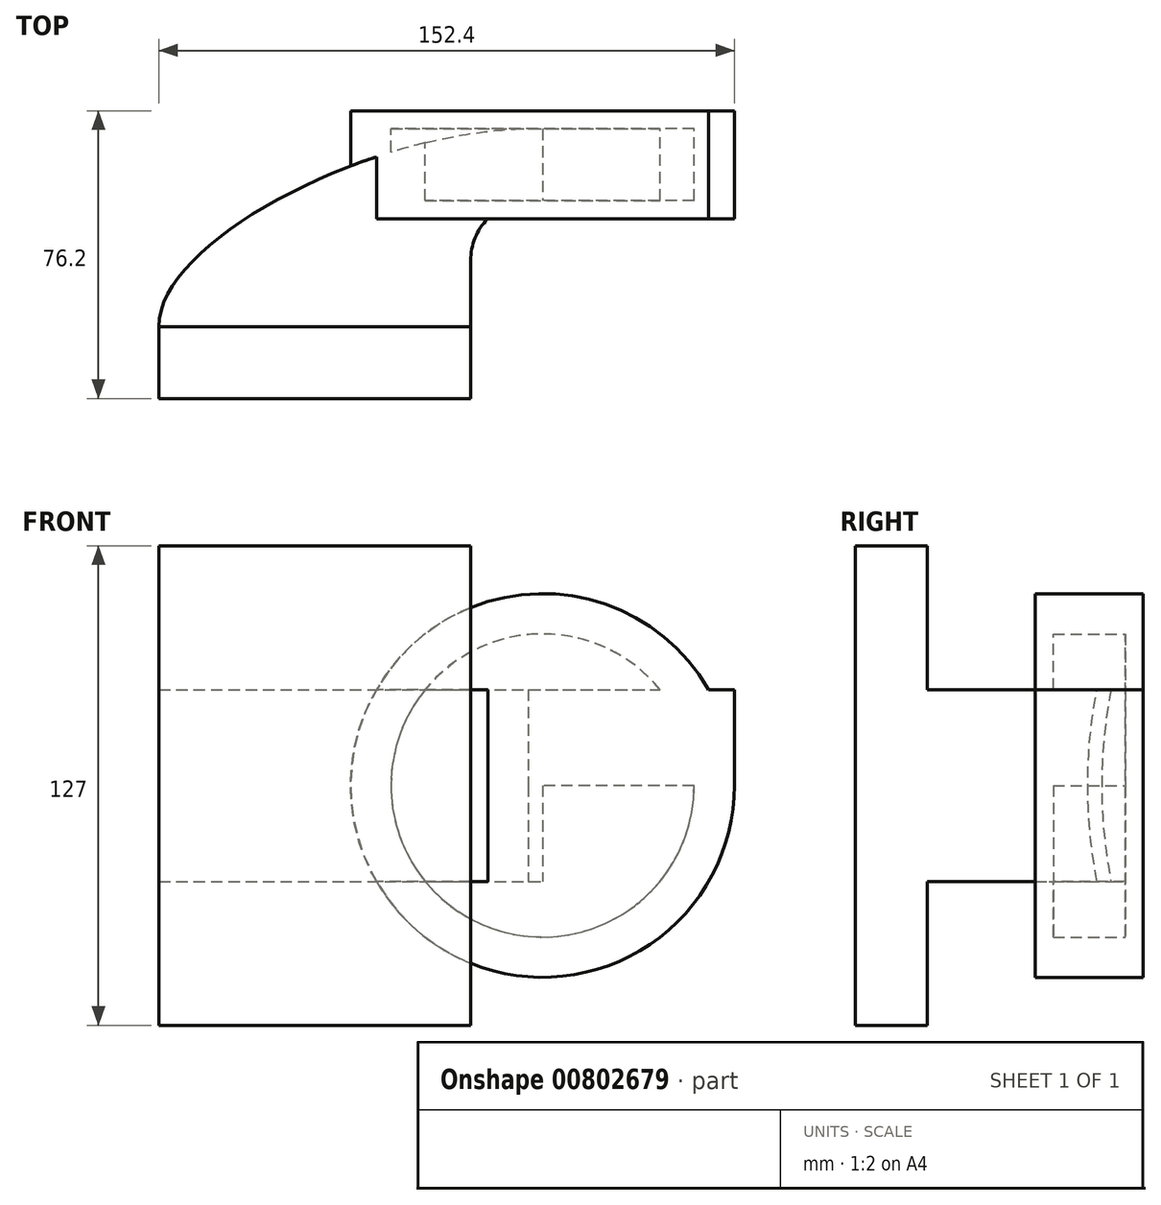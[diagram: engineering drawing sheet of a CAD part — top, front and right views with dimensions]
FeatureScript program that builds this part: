
annotation { "Feature Type Name" : "Feature", "Feature Type Description" : "" }
export const myFeature = defineFeature(function(context is Context, id is Id, definition is map)
    precondition{}
    {
        {
            var Q0;
            Q0=qCreatedBy(makeId("Top.planeOp"),FACE);
            var sketch = newSketch(context, id + "F0", { "sketchPlane" : qUnion([Q0])});
            skLineSegment(sketch, "E0.bottom", {"start": v(-38.32, 10.3) * mm, "end": v(44.23, 10.3) * mm});
            skLineSegment(sketch, "E0.top", {"start": v(-38.32, -8.76) * mm, "end": v(44.23, -8.76) * mm});
            skLineSegment(sketch, "E0.left", {"start": v(-38.32, 10.3) * mm, "end": v(-38.32, -8.76) * mm});
            skLineSegment(sketch, "E0.right", {"start": v(44.23, 10.3) * mm, "end": v(44.23, -8.76) * mm});
            skLineSegment(sketch, "E1.bottom", {"start": v(63.28, 67.44) * mm, "end": v(114.08, 67.44) * mm});
            skLineSegment(sketch, "E1.top", {"start": v(63.28, 38.87) * mm, "end": v(114.08, 38.87) * mm});
            skLineSegment(sketch, "E1.left", {"start": v(63.28, 67.44) * mm, "end": v(63.28, 38.87) * mm});
            skLineSegment(sketch, "E1.right", {"start": v(114.08, 67.44) * mm, "end": v(114.08, 38.87) * mm});
            skLineSegment(sketch, "E2", {"start": v(44.23, 10.3) * mm, "end": v(44.23, 27.77) * mm});
            skArc(sketch, "E3", {"start": v(44.23, 27.77) * mm, "mid": v(48.87, 39) * mm, "end": v(60.1, 43.64) * mm});
            skLineSegment(sketch, "E4", {"start": v(60.1, 43.64) * mm, "end": v(103.42, 43.64) * mm});
            skLineSegment(sketch, "E5.0", {"start": v(60.1, 62.7) * mm, "end": v(103.42, 62.7) * mm});
            skArc(sketch, "E5.1", {"start": v(25.18, 27.77) * mm, "mid": v(35.4, 52.46) * mm, "end": v(60.1, 62.7) * mm});
            skLineSegment(sketch, "E5.2", {"start": v(25.18, 14.52) * mm, "end": v(25.18, 27.77) * mm});
            skLineSegment(sketch, "E6", {"start": v(103.42, 43.64) * mm, "end": v(103.42, 62.7) * mm});
            skFitSpline(sketch, "E7", {"points": [v(-38.32, 10.3) * mm, v(60.1, 62.7) * mm], "startDerivative": vector(0, 69.5) * mm, "endDerivative": vector(124.45, 0.7) * mm});
            skSolve(sketch);
        }
        {
            var Q0;
            Q0=makeQuery(id+"F0.imprint","IMPRINT",FACE,{"disambiguationData":[TD([[makeQuery(id+"F0.imprint","IMPRINT",EDGE,{"derivedFrom":sQuery(id+"F0.wireOp",EDGE,"E0.bottom")}),-1.0]])]});
            extrude(context, id + "F1", {"entities" : qUnion([Q0]), "endBound" : BoundingType.SYMMETRIC, "depth" : 127 * mm, "offsetDistance" : 25.4 * mm});
        }
        {
            var Q0;
            Q0 = qSketchRegion(id + "F0", true);
            extrude(context, id + "F2", {"entities" : qUnion([Q0]), "operationType" : NewBodyOperationType.ADD, "depth" : 25.4 * mm, "offsetDistance" : 25.4 * mm});
        }
        {
            var Q0;
            Q0 = qSketchRegion(id + "F0", true);
            extrude(context, id + "F3", {"entities" : qUnion([Q0]), "operationType" : NewBodyOperationType.ADD, "depth" : 25.4 * mm, "offsetDistance" : 25.4 * mm});
        }
        {
            var Q0;
            {var subQ1=sQuery(id+"F0.wireOp",EDGE,"E0.bottom");Q0=makeQuery(id+"F0.imprint","IMPRINT",FACE,{"disambiguationData":[TD([[makeQuery(id+"F0.imprint","IMPRINT",EDGE,{"derivedFrom":subQ1}),1.0]])]});}
            extrude(context, id + "F4", {"entities" : qUnion([Q0]), "operationType" : NewBodyOperationType.ADD, "endBound" : BoundingType.SYMMETRIC, "depth" : 50.8 * mm, "offsetDistance" : 25.4 * mm});
        }
        {
            var Q0;
            {var subQ4=sQuery(id+"F0.wireOp",EDGE,"E1.bottom");Q0=makeQuery(id+"F0.imprint","IMPRINT",FACE,{"disambiguationData":[TD([[makeQuery(id+"F0.imprint","IMPRINT",EDGE,{"derivedFrom":subQ4}),-1.0]])]});}
            var Q1;
            Q1=sQuery(id+"F0.wireOp",EDGE,"E1.left");
            revolve(context, id + "F5", {"operationType" : NewBodyOperationType.ADD, "surfaceOperationType" : NewSurfaceOperationType.NEW, "entities" : qUnion([Q0]), "axis" : qUnion([Q1]), "revolveType" : RevolveType.FULL});
        }
    });
